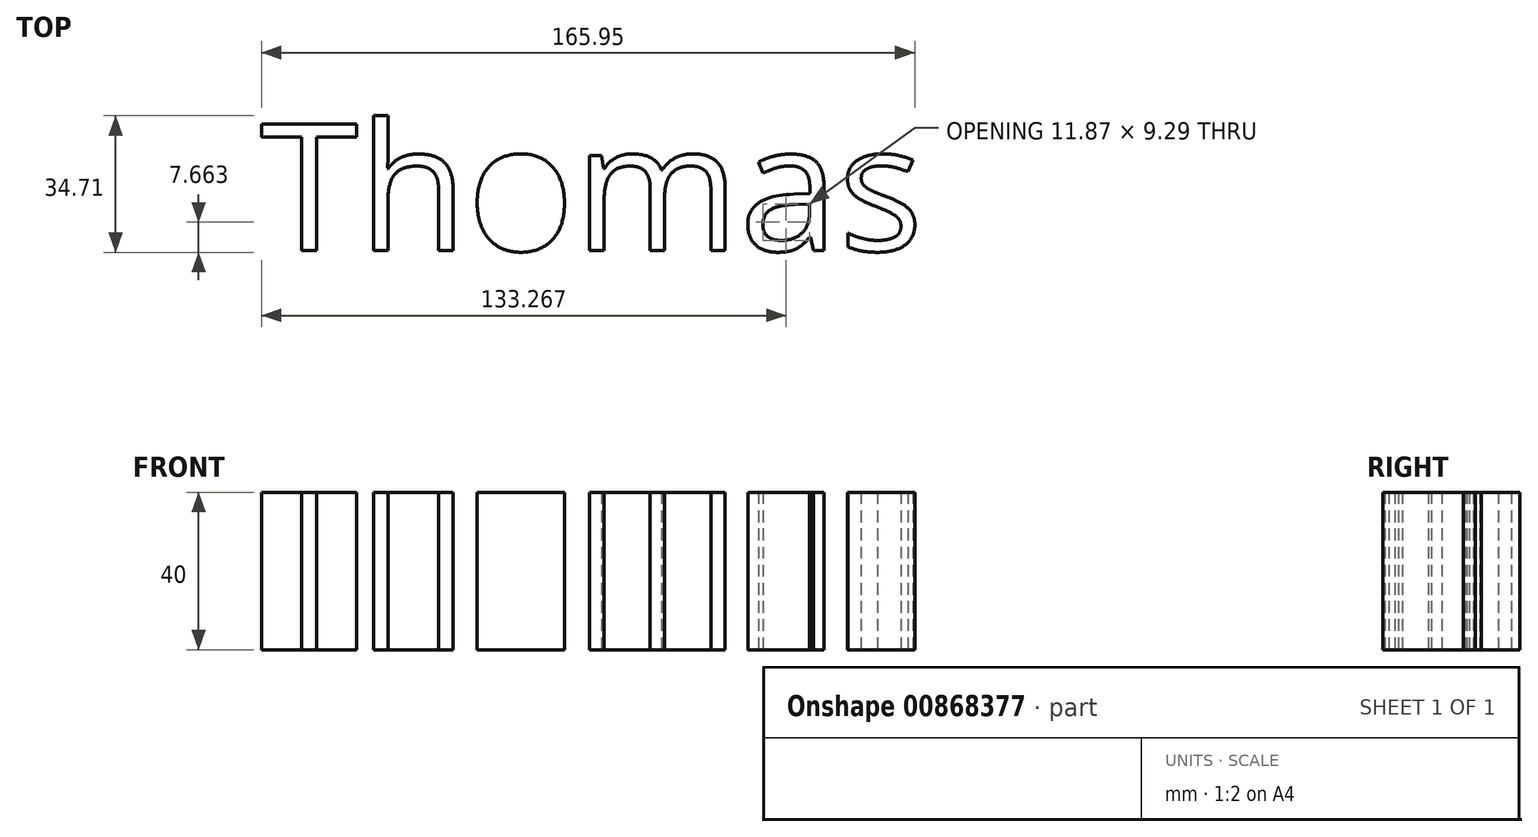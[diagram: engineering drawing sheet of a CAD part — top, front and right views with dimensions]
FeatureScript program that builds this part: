
annotation { "Feature Type Name" : "Feature", "Feature Type Description" : "" }
export const myFeature = defineFeature(function(context is Context, id is Id, definition is map)
    precondition{}
    {
        {
            var Q0;
            Q0=qCreatedBy(makeId("Top.planeOp"),FACE);
            var sketch = newSketch(context, id + "F0", { "sketchPlane" : qUnion([Q0])});
            skText(sketch, "E0", { "text": "Thomas", "fontName": "OpenSans-Regular.ttf"});
            const initialGuessF0  = {"E0": [-0.0865, 0.00905, 1, 0, 0.03247]};
            skSetInitialGuess(sketch, initialGuessF0);
            skSolve(sketch);
        }
        {
            var Q0;
            Q0=makeQuery(id+"F0.imprint","IMPRINT",FACE,{"disambiguationData":[TD([[makeQuery(id+"F0.imprint","IMPRINT",EDGE,{"derivedFrom":sQuery(id+"F0.wireOp",EDGE,"E0.sketch_text.stroke-0")}),-1.0]])]});
            var Q1;
            Q1=makeQuery(id+"F0.imprint","IMPRINT",FACE,{"disambiguationData":[TD([[makeQuery(id+"F0.imprint","IMPRINT",EDGE,{"derivedFrom":sQuery(id+"F0.wireOp",EDGE,"E0.sketch_text.stroke-8")}),-1.0]])]});
            var Q2;
            Q2=makeQuery(id+"F0.imprint","IMPRINT",FACE,{"disambiguationData":[TD([[makeQuery(id+"F0.imprint","IMPRINT",EDGE,{"derivedFrom":sQuery(id+"F0.wireOp",EDGE,"E0.sketch_text.stroke-43")}),-1.0]])]});
            var Q3;
            Q3=makeQuery(id+"F0.imprint","IMPRINT",FACE,{"disambiguationData":[TD([[makeQuery(id+"F0.imprint","IMPRINT",EDGE,{"derivedFrom":sQuery(id+"F0.wireOp",EDGE,"E0.sketch_text.stroke-98")}),-1.0]])]});
            var Q4;
            Q4=makeQuery(id+"F0.imprint","IMPRINT",FACE,{"disambiguationData":[TD([[makeQuery(id+"F0.imprint","IMPRINT",EDGE,{"derivedFrom":sQuery(id+"F0.wireOp",EDGE,"E0.sketch_text.stroke-26")}),-1.0]])]});
            var Q5;
            Q5=makeQuery(id+"F0.imprint","IMPRINT",FACE,{"disambiguationData":[TD([[makeQuery(id+"F0.imprint","IMPRINT",EDGE,{"derivedFrom":sQuery(id+"F0.wireOp",EDGE,"E0.sketch_text.stroke-71")}),-1.0]])]});
            var Q6;
            Q6=makeQuery(id+"F0.imprint","IMPRINT",FACE,{"disambiguationData":[TD([[makeQuery(id+"F0.imprint","IMPRINT",EDGE,{"derivedFrom":sQuery(id+"F0.wireOp",EDGE,"E0.sketch_text.stroke-35")}),1.0]])]});
            extrude(context, id + "F1", {"entities" : qUnion([Q0, Q1, Q2, Q3, Q4, Q5, Q6]), "depth" : 40 * mm, "offsetDistance" : 25 * mm});
        }
    });
